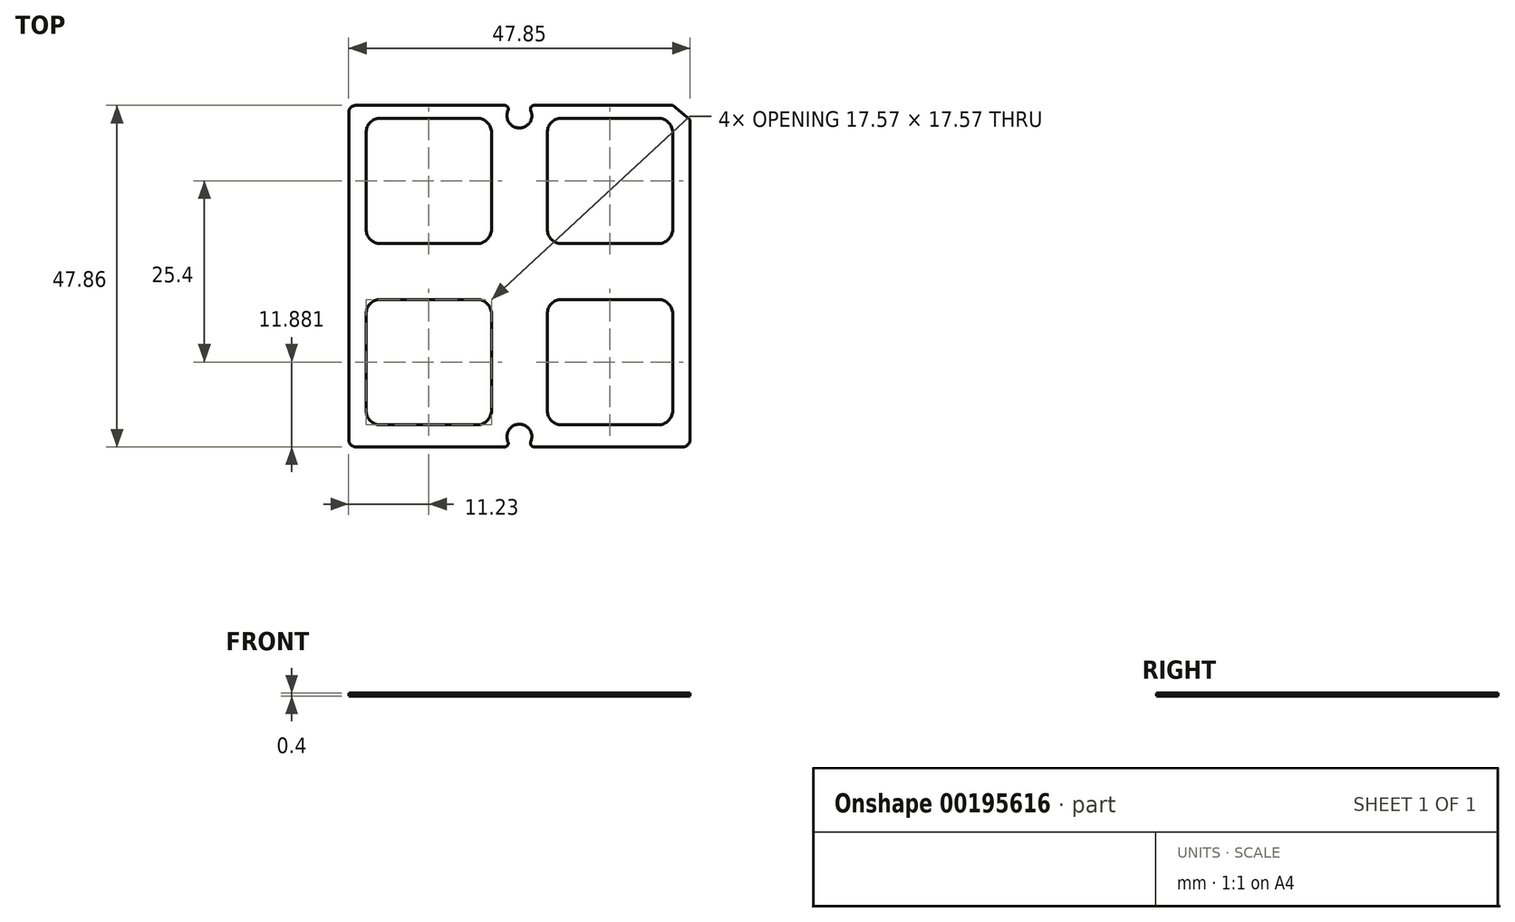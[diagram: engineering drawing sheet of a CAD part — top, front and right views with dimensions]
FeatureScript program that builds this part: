
annotation { "Feature Type Name" : "Feature", "Feature Type Description" : "" }
export const myFeature = defineFeature(function(context is Context, id is Id, definition is map)
    precondition{}
    {
        {
            var Q0;
            Q0=qCreatedBy(makeId("Top.planeOp"),FACE);
            var sketch = newSketch(context, id + "F0", { "sketchPlane" : qUnion([Q0])});
            skLineSegment(sketch, "E0.bottom", {"start": v(-22.92, -23.93) * mm, "end": v(-2.05, -23.93) * mm});
            skLineSegment(sketch, "E0.top", {"start": v(-22.93, 23.93) * mm, "end": v(-2.05, 23.93) * mm});
            skLineSegment(sketch, "E0.left", {"start": v(-23.92, -22.93) * mm, "end": v(-23.93, 22.92) * mm});
            skLineSegment(sketch, "E0.right", {"start": v(23.93, -22.93) * mm, "end": v(23.92, 21.89) * mm});
            skPoint(sketch, "E0.middle", {"position": v(0, 0) * mm});
            skLineSegment(sketch, "E1.bottom", {"start": v(-19.48, -20.83) * mm, "end": v(-5.92, -20.83) * mm});
            skLineSegment(sketch, "E1.top", {"start": v(-19.49, -3.26) * mm, "end": v(-5.91, -3.26) * mm});
            skLineSegment(sketch, "E1.left", {"start": v(-21.48, -18.83) * mm, "end": v(-21.48, -5.26) * mm});
            skLineSegment(sketch, "E1.right", {"start": v(-3.91, -18.83) * mm, "end": v(-3.91, -5.26) * mm});
            skPoint(sketch, "E1.middle", {"position": v(-12.7, -12.05) * mm});
            skLineSegment(sketch, "E2.bottom", {"start": v(-19.48, 4.57) * mm, "end": v(-5.92, 4.57) * mm});
            skLineSegment(sketch, "E2.top", {"start": v(-19.48, 22.14) * mm, "end": v(-5.92, 22.14) * mm});
            skLineSegment(sketch, "E2.left", {"start": v(-21.48, 6.57) * mm, "end": v(-21.48, 20.14) * mm});
            skLineSegment(sketch, "E2.right", {"start": v(-3.91, 6.57) * mm, "end": v(-3.91, 20.14) * mm});
            skPoint(sketch, "E2.middle", {"position": v(-12.7, 13.35) * mm});
            skLineSegment(sketch, "E3.MirrorCS", {"start": v(19.48, 22.14) * mm, "end": v(5.92, 22.14) * mm});
            skLineSegment(sketch, "E4.MirrorCS", {"start": v(3.91, 6.57) * mm, "end": v(3.91, 20.14) * mm});
            skLineSegment(sketch, "E5.MirrorCS", {"start": v(21.48, 6.57) * mm, "end": v(21.48, 20.14) * mm});
            skLineSegment(sketch, "E6.MirrorCS", {"start": v(19.48, 4.57) * mm, "end": v(5.92, 4.57) * mm});
            skLineSegment(sketch, "E7.MirrorCS", {"start": v(19.48, -3.26) * mm, "end": v(5.92, -3.26) * mm});
            skLineSegment(sketch, "E8.MirrorCS", {"start": v(21.48, -18.83) * mm, "end": v(21.48, -5.26) * mm});
            skLineSegment(sketch, "E9.MirrorCS", {"start": v(19.48, -20.83) * mm, "end": v(5.92, -20.83) * mm});
            skLineSegment(sketch, "E10.MirrorCS", {"start": v(3.91, -18.83) * mm, "end": v(3.91, -5.26) * mm});
            skArc(sketch, "E11", {"start": v(-1.6, 23.22) * mm, "mid": v(0, 20.75) * mm, "end": v(1.6, 23.22) * mm});
            skPoint(sketch, "E11.centerSnap0", {"position": v(0, 23.93) * mm});
            skArc(sketch, "E12", {"start": v(1.6, -23.22) * mm, "mid": v(0, -20.75) * mm, "end": v(-1.6, -23.22) * mm});
            skLineSegment(sketch, "E13.trimOffspring", {"start": v(2.05, -23.93) * mm, "end": v(22.93, -23.93) * mm});
            skLineSegment(sketch, "E14.trimOffspring", {"start": v(2.05, 23.93) * mm, "end": v(21.48, 23.93) * mm});
            skPoint(sketch, "E15.visualSharp", {"position": v(-1.02, 23.93) * mm});
            skArc(sketch, "E15.filletArc", {"start": v(-1.6, 23.22) * mm, "mid": v(-1.63, 23.7) * mm, "end": v(-2.05, 23.93) * mm});
            skPoint(sketch, "E16.visualSharp", {"position": v(1.02, 23.93) * mm});
            skArc(sketch, "E16.filletArc", {"start": v(2.05, 23.93) * mm, "mid": v(1.63, 23.7) * mm, "end": v(1.6, 23.22) * mm});
            skPoint(sketch, "E17.visualSharp", {"position": v(-1.02, -23.93) * mm});
            skArc(sketch, "E17.filletArc", {"start": v(-2.05, -23.93) * mm, "mid": v(-1.63, -23.7) * mm, "end": v(-1.6, -23.22) * mm});
            skPoint(sketch, "E18.visualSharp", {"position": v(1.02, -23.93) * mm});
            skArc(sketch, "E18.filletArc", {"start": v(1.6, -23.22) * mm, "mid": v(1.63, -23.7) * mm, "end": v(2.05, -23.93) * mm});
            skPoint(sketch, "E19.visualSharp", {"position": v(-21.48, -3.26) * mm});
            skArc(sketch, "E19.filletArc", {"start": v(-19.49, -3.26) * mm, "mid": v(-20.9, -3.85) * mm, "end": v(-21.48, -5.26) * mm});
            skPoint(sketch, "E20.visualSharp", {"position": v(-3.91, -3.26) * mm});
            skArc(sketch, "E20.filletArc", {"start": v(-3.91, -5.26) * mm, "mid": v(-4.5, -3.85) * mm, "end": v(-5.91, -3.26) * mm});
            skPoint(sketch, "E21.visualSharp", {"position": v(-3.91, -20.83) * mm});
            skArc(sketch, "E21.filletArc", {"start": v(-5.92, -20.83) * mm, "mid": v(-4.5, -20.25) * mm, "end": v(-3.91, -18.83) * mm});
            skPoint(sketch, "E22.visualSharp", {"position": v(-21.48, -20.83) * mm});
            skArc(sketch, "E22.filletArc", {"start": v(-21.48, -18.83) * mm, "mid": v(-20.9, -20.25) * mm, "end": v(-19.48, -20.83) * mm});
            skPoint(sketch, "E23.visualSharp", {"position": v(3.91, -20.83) * mm});
            skArc(sketch, "E23.filletArc", {"start": v(3.91, -18.83) * mm, "mid": v(4.5, -20.25) * mm, "end": v(5.92, -20.83) * mm});
            skPoint(sketch, "E24.visualSharp", {"position": v(21.48, -20.83) * mm});
            skArc(sketch, "E24.filletArc", {"start": v(19.48, -20.83) * mm, "mid": v(20.9, -20.25) * mm, "end": v(21.49, -18.83) * mm});
            skPoint(sketch, "E25.visualSharp", {"position": v(21.48, -3.26) * mm});
            skArc(sketch, "E25.filletArc", {"start": v(21.48, -5.26) * mm, "mid": v(20.9, -3.85) * mm, "end": v(19.48, -3.26) * mm});
            skPoint(sketch, "E26.visualSharp", {"position": v(3.91, -3.26) * mm});
            skArc(sketch, "E26.filletArc", {"start": v(5.92, -3.26) * mm, "mid": v(4.5, -3.85) * mm, "end": v(3.91, -5.26) * mm});
            skPoint(sketch, "E27.visualSharp", {"position": v(3.91, 4.57) * mm});
            skArc(sketch, "E27.filletArc", {"start": v(3.91, 6.57) * mm, "mid": v(4.5, 5.15) * mm, "end": v(5.92, 4.57) * mm});
            skPoint(sketch, "E28.visualSharp", {"position": v(21.48, 4.57) * mm});
            skArc(sketch, "E28.filletArc", {"start": v(19.48, 4.57) * mm, "mid": v(20.9, 5.15) * mm, "end": v(21.48, 6.57) * mm});
            skPoint(sketch, "E29.visualSharp", {"position": v(-3.91, 22.14) * mm});
            skArc(sketch, "E29.filletArc", {"start": v(-3.91, 20.14) * mm, "mid": v(-4.5, 21.55) * mm, "end": v(-5.92, 22.14) * mm});
            skPoint(sketch, "E30.visualSharp", {"position": v(-21.48, 22.14) * mm});
            skArc(sketch, "E30.filletArc", {"start": v(-19.48, 22.14) * mm, "mid": v(-20.9, 21.55) * mm, "end": v(-21.49, 20.14) * mm});
            skPoint(sketch, "E31.visualSharp", {"position": v(-21.48, 4.57) * mm});
            skArc(sketch, "E31.filletArc", {"start": v(-21.48, 6.57) * mm, "mid": v(-20.9, 5.15) * mm, "end": v(-19.48, 4.57) * mm});
            skPoint(sketch, "E32.visualSharp", {"position": v(-3.91, 4.57) * mm});
            skArc(sketch, "E32.filletArc", {"start": v(-5.92, 4.57) * mm, "mid": v(-4.5, 5.15) * mm, "end": v(-3.91, 6.57) * mm});
            skPoint(sketch, "E33.visualSharp", {"position": v(3.92, 22.14) * mm});
            skArc(sketch, "E33.filletArc", {"start": v(5.92, 22.14) * mm, "mid": v(4.5, 21.55) * mm, "end": v(3.92, 20.14) * mm});
            skPoint(sketch, "E34.visualSharp", {"position": v(21.48, 22.14) * mm});
            skArc(sketch, "E34.filletArc", {"start": v(21.48, 20.14) * mm, "mid": v(20.9, 21.55) * mm, "end": v(19.48, 22.14) * mm});
            skPoint(sketch, "E35.visualSharp", {"position": v(-23.93, 23.93) * mm});
            skArc(sketch, "E35.filletArc", {"start": v(-22.93, 23.92) * mm, "mid": v(-23.63, 23.63) * mm, "end": v(-23.93, 22.92) * mm});
            skPoint(sketch, "E36.visualSharp", {"position": v(-23.92, -23.93) * mm});
            skArc(sketch, "E36.filletArc", {"start": v(-23.92, -22.93) * mm, "mid": v(-23.63, -23.63) * mm, "end": v(-22.92, -23.93) * mm});
            skPoint(sketch, "E37.visualSharp", {"position": v(23.93, -23.93) * mm});
            skArc(sketch, "E37.filletArc", {"start": v(22.93, -23.93) * mm, "mid": v(23.63, -23.63) * mm, "end": v(23.93, -22.93) * mm});
            skLineSegment(sketch, "E38", {"start": v(21.48, 23.93) * mm, "end": v(23.92, 21.89) * mm});
            skPoint(sketch, "E39.orphan", {"position": v(23.92, 23.93) * mm});
            skSolve(sketch);
        }
        {
            var Q0;
            Q0 = qSketchRegion(id + "F0", true);
            extrude(context, id + "F1", {"entities" : qUnion([Q0]), "endBound" : BoundingType.SYMMETRIC, "depth" : 0.4 * mm});
        }
    });
